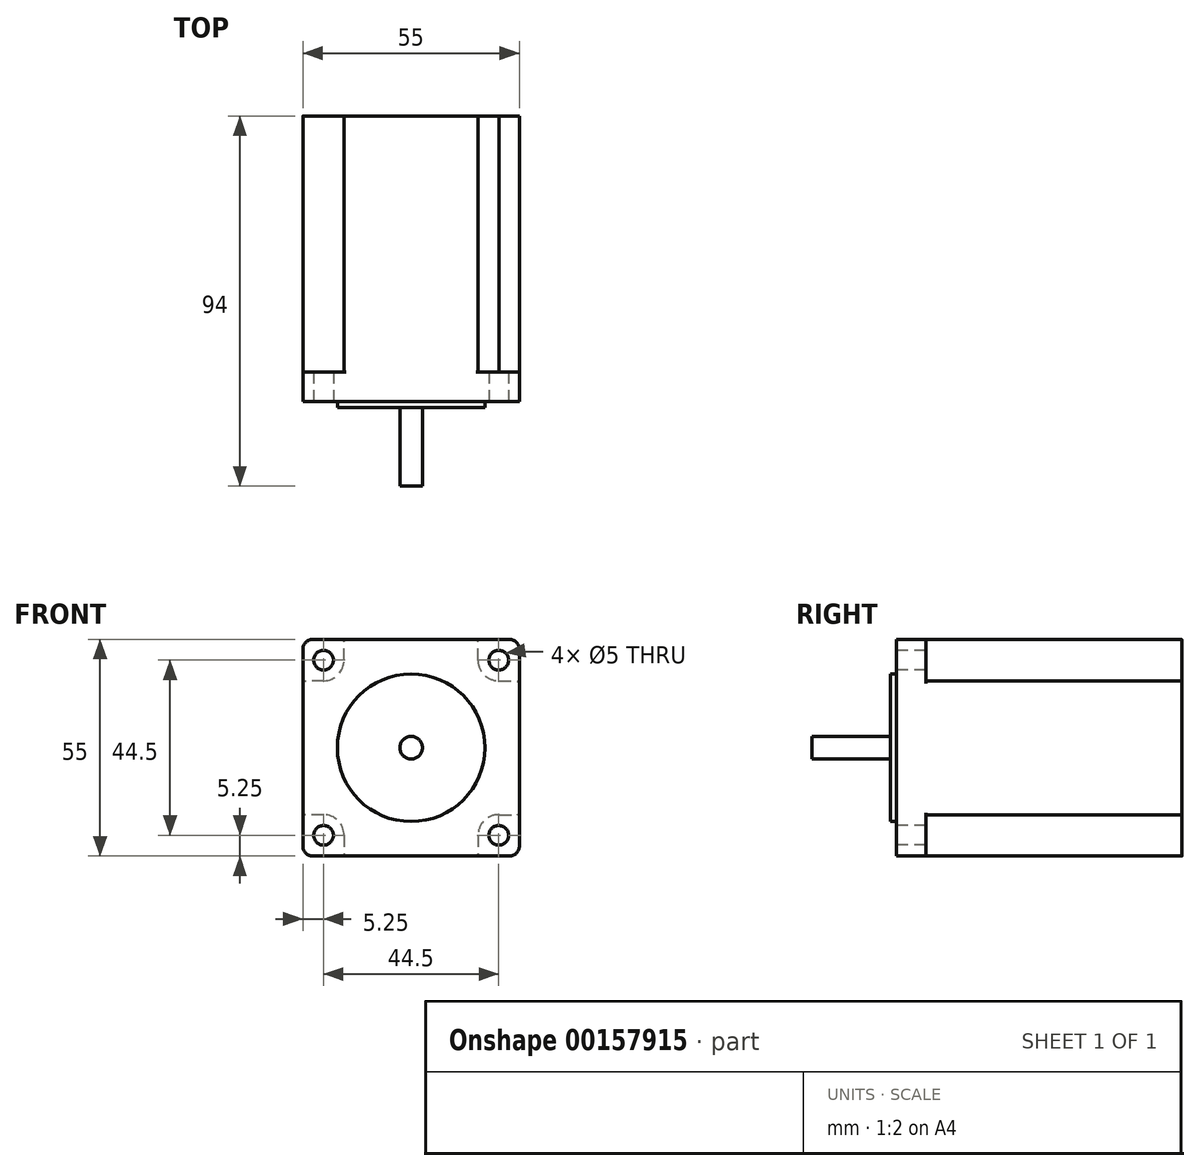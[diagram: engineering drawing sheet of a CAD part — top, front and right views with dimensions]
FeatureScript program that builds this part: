
annotation { "Feature Type Name" : "Feature", "Feature Type Description" : "" }
export const myFeature = defineFeature(function(context is Context, id is Id, definition is map)
    precondition{}
    {
        {
            var Q0;
            Q0=qCreatedBy(makeId("Front.planeOp"),FACE);
            var sketch = newSketch(context, id + "F0", { "sketchPlane" : qUnion([Q0])});
            skLineSegment(sketch, "E0.bottom", {"start": v(-25, 27.5) * mm, "end": v(25, 27.5) * mm});
            skLineSegment(sketch, "E0.top", {"start": v(-25, -27.5) * mm, "end": v(25, -27.5) * mm});
            skLineSegment(sketch, "E0.left", {"start": v(-27.5, 25) * mm, "end": v(-27.5, -25) * mm});
            skLineSegment(sketch, "E0.right", {"start": v(27.5, 25) * mm, "end": v(27.5, -25) * mm});
            skPoint(sketch, "E1.visualSharp", {"position": v(27.5, 27.5) * mm});
            skArc(sketch, "E1.filletArc", {"start": v(27.5, 25) * mm, "mid": v(26.77, 26.77) * mm, "end": v(25, 27.5) * mm});
            skPoint(sketch, "E2.visualSharp", {"position": v(27.5, -27.5) * mm});
            skArc(sketch, "E2.filletArc", {"start": v(25, -27.5) * mm, "mid": v(26.77, -26.77) * mm, "end": v(27.5, -25) * mm});
            skPoint(sketch, "E3.visualSharp", {"position": v(-27.5, -27.5) * mm});
            skArc(sketch, "E3.filletArc", {"start": v(-27.5, -25) * mm, "mid": v(-26.77, -26.77) * mm, "end": v(-25, -27.5) * mm});
            skPoint(sketch, "E4.visualSharp", {"position": v(-27.5, 27.5) * mm});
            skArc(sketch, "E4.filletArc", {"start": v(-25, 27.5) * mm, "mid": v(-26.77, 26.77) * mm, "end": v(-27.5, 25) * mm});
            skCircle(sketch, "E5", {"center": v(22.25, 22.25) * mm, "radius": 2.5 * mm});
            skCircle(sketch, "E6.MirrorC", {"center": v(22.25, -22.25) * mm, "radius": 2.5 * mm});
            skCircle(sketch, "E7.MirrorC", {"center": v(-22.25, -22.25) * mm, "radius": 2.5 * mm});
            skCircle(sketch, "E8.MirrorC", {"center": v(-22.25, 22.25) * mm, "radius": 2.5 * mm});
            skCircle(sketch, "E9", {"center": v(0, 0) * mm, "radius": 18.75 * mm});
            skSolve(sketch);
        }
        {
            var Q0;
            Q0=makeQuery(id+"F0.imprint","IMPRINT",FACE,{"disambiguationData":[TD([[makeQuery(id+"F0.imprint","IMPRINT",EDGE,{"derivedFrom":sQuery(id+"F0.wireOp",EDGE,"E9")}),1.0]])]});
            extrude(context, id + "F1", {"entities" : qUnion([Q0]), "offsetDistance" : 25 * mm, "depth" : 1.5 * mm});
        }
        {
            var Q0;
            Q0=makeQuery(id+"F0.imprint","IMPRINT",FACE,{"disambiguationData":[TD([[makeQuery(id+"F0.imprint","IMPRINT",EDGE,{"derivedFrom":sQuery(id+"F0.wireOp",EDGE,"E0.bottom")}),-1.0]])]});
            var Q1;
            Q1=makeQuery(id+"F0.imprint","IMPRINT",FACE,{"disambiguationData":[TD([[makeQuery(id+"F0.imprint","IMPRINT",EDGE,{"derivedFrom":sQuery(id+"F0.wireOp",EDGE,"E9")}),1.0]])]});
            extrude(context, id + "F2", {"entities" : qUnion([Q0, Q1]), "operationType" : NewBodyOperationType.ADD, "oppositeDirection" : true, "offsetDistance" : 25 * mm, "depth" : 7.5 * mm});
        }
        {
            var Q0;
            Q0=makeQuery(id+"F2.opExtrude","CAP_FACE",FACE,{"disambiguationData":[OSD([sQuery(id+"F0.wireOp",EDGE,"E0.bottom"),sQuery(id+"F0.wireOp",EDGE,"E0.top"),sQuery(id+"F0.wireOp",EDGE,"E0.left"),sQuery(id+"F0.wireOp",EDGE,"E0.right"),sQuery(id+"F0.wireOp",EDGE,"E1.filletArc"),sQuery(id+"F0.wireOp",EDGE,"E2.filletArc"),sQuery(id+"F0.wireOp",EDGE,"E3.filletArc"),sQuery(id+"F0.wireOp",EDGE,"E4.filletArc"),sQuery(id+"F0.wireOp",EDGE,"E6.MirrorC"),sQuery(id+"F0.wireOp",EDGE,"E5"),sQuery(id+"F0.wireOp",EDGE,"E7.MirrorC"),sQuery(id+"F0.wireOp",EDGE,"E8.MirrorC")])],"isStart":false});
            var sketch = newSketch(context, id + "F3", { "sketchPlane" : qUnion([Q0])});
            skLineSegment(sketch, "E10.0", {"start": v(27.5, 16.87) * mm, "end": v(27.5, -17) * mm});
            skLineSegment(sketch, "E11.0", {"start": v(17, 27.5) * mm, "end": v(-17, 27.5) * mm});
            skLineSegment(sketch, "E12.0", {"start": v(17, -27.5) * mm, "end": v(-17, -27.5) * mm});
            skLineSegment(sketch, "E13.0", {"start": v(-27.5, 16.87) * mm, "end": v(-27.5, -17) * mm});
            skArc(sketch, "E14", {"start": v(17, 22.25) * mm, "mid": v(18.5, 18.59) * mm, "end": v(22.12, 17) * mm});
            skArc(sketch, "E15.MirrorCS", {"start": v(-17, 22.25) * mm, "mid": v(-18.56, 18.51) * mm, "end": v(-22.32, 17) * mm});
            skArc(sketch, "E16.MirrorCS", {"start": v(17, -22.25) * mm, "mid": v(18.54, -18.54) * mm, "end": v(22.25, -17) * mm});
            skArc(sketch, "E17.MirrorCS", {"start": v(-17, -22.25) * mm, "mid": v(-18.6, -18.47) * mm, "end": v(-22.45, -17) * mm});
            skLineSegment(sketch, "E18", {"start": v(22.12, 17) * mm, "end": v(27.5, 16.87) * mm});
            skLineSegment(sketch, "E19", {"start": v(17, 22.25) * mm, "end": v(17, 27.5) * mm});
            skLineSegment(sketch, "E20.MirrorCS", {"start": v(17, -22.25) * mm, "end": v(17, -27.5) * mm});
            skLineSegment(sketch, "E21", {"start": v(22.25, -17) * mm, "end": v(27.5, -17) * mm});
            skLineSegment(sketch, "E22.MirrorCS", {"start": v(-17, 22.25) * mm, "end": v(-17, 27.5) * mm});
            skLineSegment(sketch, "E23.MirrorCS", {"start": v(-22.12, 17) * mm, "end": v(-27.5, 16.87) * mm});
            skLineSegment(sketch, "E24.MirrorCS", {"start": v(-22.25, -17) * mm, "end": v(-27.5, -17) * mm});
            skLineSegment(sketch, "E25.MirrorCS", {"start": v(-17, -22.25) * mm, "end": v(-17, -27.5) * mm});
            skPoint(sketch, "E26.orphan", {"position": v(-27.5, 22.25) * mm});
            skPoint(sketch, "E27.orphan", {"position": v(-22.25, 27.5) * mm});
            skPoint(sketch, "E28.orphan", {"position": v(-27.5, -22.25) * mm});
            skPoint(sketch, "E29.orphan", {"position": v(-22.25, -27.5) * mm});
            skSolve(sketch);
        }
        {
            var Q0;
            Q0 = qSketchRegion(id + "F3", true);
            extrude(context, id + "F4", {"entities" : qUnion([Q0]), "operationType" : NewBodyOperationType.ADD, "offsetDistance" : 25 * mm, "depth" : 65 * mm});
        }
        {
            var Q0;
            Q0=makeQuery(id+"F4.opExtrude","SWEPT_EDGE",EDGE,{"disambiguationData":[OSD([sQuery(id+"F0.wireOp",EDGE,"E0.bottom"),sQuery(id+"F3.wireOp",EDGE,"E11.0"),sQuery(id+"F3.wireOp",EDGE,"E15.MirrorCS")])]});
            var Q1;
            Q1=makeQuery(id+"F4.opExtrude","SWEPT_EDGE",EDGE,{"disambiguationData":[OSD([sQuery(id+"F0.wireOp",EDGE,"E0.right"),sQuery(id+"F3.wireOp",EDGE,"E13.0"),sQuery(id+"F3.wireOp",EDGE,"E15.MirrorCS")])]});
            var Q2;
            Q2=makeQuery(id+"F4.opExtrude","SWEPT_EDGE",EDGE,{"disambiguationData":[OSD([sQuery(id+"F0.wireOp",EDGE,"E0.bottom"),sQuery(id+"F3.wireOp",EDGE,"E11.0"),sQuery(id+"F3.wireOp",EDGE,"E14")])]});
            var Q3;
            Q3=makeQuery(id+"F4.opExtrude","SWEPT_EDGE",EDGE,{"disambiguationData":[OSD([sQuery(id+"F0.wireOp",EDGE,"E0.left"),sQuery(id+"F3.wireOp",EDGE,"E10.0"),sQuery(id+"F3.wireOp",EDGE,"E14")])]});
            var Q4;
            Q4=makeQuery(id+"F4.opExtrude","SWEPT_EDGE",EDGE,{"disambiguationData":[OSD([sQuery(id+"F0.wireOp",EDGE,"E0.left"),sQuery(id+"F3.wireOp",EDGE,"E10.0"),sQuery(id+"F3.wireOp",EDGE,"E16.MirrorCS")])]});
            var Q5;
            Q5=makeQuery(id+"F4.opExtrude","SWEPT_EDGE",EDGE,{"disambiguationData":[OSD([sQuery(id+"F0.wireOp",EDGE,"E0.top"),sQuery(id+"F3.wireOp",EDGE,"E12.0"),sQuery(id+"F3.wireOp",EDGE,"E16.MirrorCS")])]});
            var Q6;
            Q6=makeQuery(id+"F4.opExtrude","SWEPT_EDGE",EDGE,{"disambiguationData":[OSD([sQuery(id+"F0.wireOp",EDGE,"E0.top"),sQuery(id+"F3.wireOp",EDGE,"E12.0"),sQuery(id+"F3.wireOp",EDGE,"E17.MirrorCS")])]});
            var Q7;
            Q7=makeQuery(id+"F4.opExtrude","SWEPT_EDGE",EDGE,{"disambiguationData":[OSD([sQuery(id+"F0.wireOp",EDGE,"E0.right"),sQuery(id+"F3.wireOp",EDGE,"E13.0"),sQuery(id+"F3.wireOp",EDGE,"E17.MirrorCS")])]});
            fillet(context, id + "F5", {"entities" : qUnion([Q0, Q1, Q2, Q3, Q4, Q5, Q6, Q7]), "radius" : 0.5 * mm, "tangentPropagation" : true, "allowEdgeOverflow" : false});
        }
        {
            var Q0;
            Q0=makeQuery(id+"F1.opExtrude","CAP_FACE",FACE,{"disambiguationData":[OSD([sQuery(id+"F0.wireOp",EDGE,"E9")])],"isStart":false});
            var sketch = newSketch(context, id + "F6", { "sketchPlane" : qUnion([Q0])});
            skCircle(sketch, "E30", {"center": v(0, 0) * mm, "radius": 2.88 * mm});
            skSolve(sketch);
        }
        {
            var Q0;
            Q0 = qSketchRegion(id + "F6", true);
            extrude(context, id + "F7", {"entities" : qUnion([Q0]), "operationType" : NewBodyOperationType.ADD, "offsetDistance" : 25 * mm, "depth" : 20 * mm});
        }
    });
